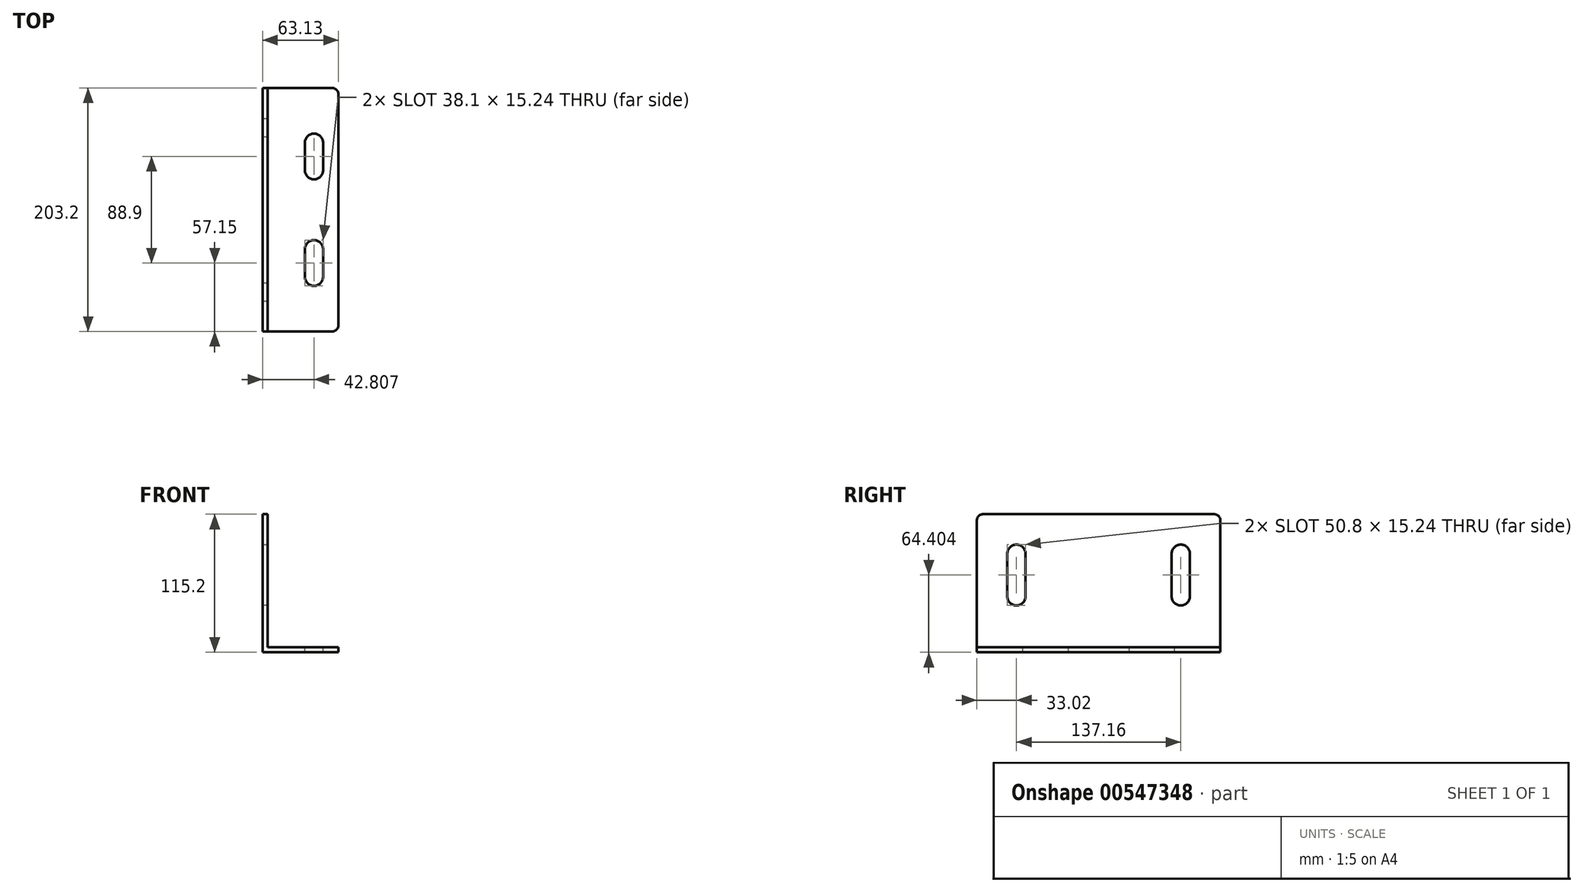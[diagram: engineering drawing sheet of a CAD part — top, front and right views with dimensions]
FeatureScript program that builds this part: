
annotation { "Feature Type Name" : "Feature", "Feature Type Description" : "" }
export const myFeature = defineFeature(function(context is Context, id is Id, definition is map)
    precondition{}
    {
        {
            var Q0;
            Q0=qCreatedBy(makeId("Front.planeOp"),FACE);
            var sketch = newSketch(context, id + "F0", { "sketchPlane" : qUnion([Q0])});
            skLineSegment(sketch, "E0", {"start": v(0, 0) * mm, "end": v(0, 111.1) * mm});
            skLineSegment(sketch, "E1", {"start": v(0, 0) * mm, "end": v(59.18, 0) * mm});
            skLineSegment(sketch, "E2", {"start": v(59.18, 0) * mm, "end": v(59.18, -4.11) * mm});
            skLineSegment(sketch, "E3", {"start": v(59.18, -4.11) * mm, "end": v(-3.95, -4.11) * mm});
            skLineSegment(sketch, "E4", {"start": v(-3.95, -4.11) * mm, "end": v(-3.95, 111.1) * mm});
            skLineSegment(sketch, "E5", {"start": v(-3.95, 111.1) * mm, "end": v(0, 111.1) * mm});
            skSolve(sketch);
        }
        {
            var Q0;
            Q0=makeQuery(id+"F0.imprint","IMPRINT",FACE,{"disambiguationData":[TD([[makeQuery(id+"F0.imprint","IMPRINT",EDGE,{"derivedFrom":sQuery(id+"F0.wireOp",EDGE,"E0")}),1.0]])]});
            extrude(context, id + "F1", {"entities" : qUnion([Q0]), "depth" : 203.2 * mm, "offsetDistance" : 25.4 * mm});
        }
        {
            var Q0;
            Q0=makeQuery(id+"F1.opExtrude","CAP_EDGE",EDGE,{"disambiguationData":[OSD([sQuery(id+"F0.wireOp",EDGE,"E5")])],"isStart":false});
            var Q1;
            Q1=makeQuery(id+"F1.opExtrude","CAP_EDGE",EDGE,{"disambiguationData":[OSD([sQuery(id+"F0.wireOp",EDGE,"E2")])],"isStart":false});
            var Q2;
            Q2=makeQuery(id+"F1.opExtrude","CAP_EDGE",EDGE,{"disambiguationData":[OSD([sQuery(id+"F0.wireOp",EDGE,"E2")])],"isStart":true});
            var Q3;
            Q3=makeQuery(id+"F1.opExtrude","CAP_EDGE",EDGE,{"disambiguationData":[OSD([sQuery(id+"F0.wireOp",EDGE,"E5")])],"isStart":true});
            fillet(context, id + "F2", {"entities" : qUnion([Q0, Q1, Q2, Q3]), "radius" : 5.08 * mm, "tangentPropagation" : true, "allowEdgeOverflow" : false});
        }
        {
            var Q0;
            Q0=makeQuery(id+"F1.opExtrude","SWEPT_FACE",FACE,{"disambiguationData":[OSD([sQuery(id+"F0.wireOp",EDGE,"E0")])]});
            var sketch = newSketch(context, id + "F3", { "sketchPlane" : qUnion([Q0])});
            skLineSegment(sketch, "E6.bottom", {"start": v(-177.8, 85.7) * mm, "end": v(-162.56, 85.7) * mm});
            skLineSegment(sketch, "E6.top", {"start": v(-177.8, 34.9) * mm, "end": v(-162.56, 34.9) * mm});
            skLineSegment(sketch, "E6.left", {"start": v(-177.8, 85.7) * mm, "end": v(-177.8, 34.9) * mm});
            skLineSegment(sketch, "E6.right", {"start": v(-162.56, 85.7) * mm, "end": v(-162.56, 34.9) * mm});
            skLineSegment(sketch, "E7.bottom", {"start": v(-40.64, 85.7) * mm, "end": v(-25.4, 85.7) * mm});
            skLineSegment(sketch, "E7.top", {"start": v(-40.64, 34.9) * mm, "end": v(-25.4, 34.9) * mm});
            skLineSegment(sketch, "E7.left", {"start": v(-40.64, 85.7) * mm, "end": v(-40.64, 34.9) * mm});
            skLineSegment(sketch, "E7.right", {"start": v(-25.4, 85.7) * mm, "end": v(-25.4, 34.9) * mm});
            skSolve(sketch);
        }
        {
            var Q0;
            Q0=makeQuery(id+"F3.imprint","IMPRINT",FACE,{"disambiguationData":[TD([[makeQuery(id+"F3.imprint","IMPRINT",EDGE,{"derivedFrom":sQuery(id+"F3.wireOp",EDGE,"E6.bottom")}),-1.0]])]});
            var Q1;
            Q1=makeQuery(id+"F3.imprint","IMPRINT",FACE,{"disambiguationData":[TD([[makeQuery(id+"F3.imprint","IMPRINT",EDGE,{"derivedFrom":sQuery(id+"F3.wireOp",EDGE,"E7.bottom")}),-1.0]])]});
            extrude(context, id + "F4", {"entities" : qUnion([Q0, Q1]), "operationType" : NewBodyOperationType.REMOVE, "endBound" : BoundingType.UP_TO_NEXT, "oppositeDirection" : true, "depth" : 25.4 * mm, "offsetDistance" : 25.4 * mm});
        }
        {
            var Q0;
            Q0=makeQuery(id+"F4.boolean.opBoolean","COPY",EDGE,{"derivedFrom":makeQuery(id+"F4.opExtrude","SWEPT_EDGE",EDGE,{"disambiguationData":[OSD([sQuery(id+"F3.wireOp",EDGE,"E6.top"),sQuery(id+"F3.wireOp",EDGE,"E6.left")])]})});
            var Q1;
            Q1=makeQuery(id+"F4.boolean.opBoolean","COPY",EDGE,{"derivedFrom":makeQuery(id+"F4.opExtrude","SWEPT_EDGE",EDGE,{"disambiguationData":[OSD([sQuery(id+"F3.wireOp",EDGE,"E6.top"),sQuery(id+"F3.wireOp",EDGE,"E6.right")])]})});
            var Q2;
            Q2=makeQuery(id+"F4.boolean.opBoolean","COPY",EDGE,{"derivedFrom":makeQuery(id+"F4.opExtrude","SWEPT_EDGE",EDGE,{"disambiguationData":[OSD([sQuery(id+"F3.wireOp",EDGE,"E6.bottom"),sQuery(id+"F3.wireOp",EDGE,"E6.left")])]})});
            var Q3;
            Q3=makeQuery(id+"F4.boolean.opBoolean","COPY",EDGE,{"derivedFrom":makeQuery(id+"F4.opExtrude","SWEPT_EDGE",EDGE,{"disambiguationData":[OSD([sQuery(id+"F3.wireOp",EDGE,"E6.bottom"),sQuery(id+"F3.wireOp",EDGE,"E6.right")])]})});
            var Q4;
            Q4=makeQuery(id+"F4.boolean.opBoolean","COPY",EDGE,{"derivedFrom":makeQuery(id+"F4.opExtrude","SWEPT_EDGE",EDGE,{"disambiguationData":[OSD([sQuery(id+"F3.wireOp",EDGE,"E7.bottom"),sQuery(id+"F3.wireOp",EDGE,"E7.left")])]})});
            var Q5;
            Q5=makeQuery(id+"F4.boolean.opBoolean","COPY",EDGE,{"derivedFrom":makeQuery(id+"F4.opExtrude","SWEPT_EDGE",EDGE,{"disambiguationData":[OSD([sQuery(id+"F3.wireOp",EDGE,"E7.bottom"),sQuery(id+"F3.wireOp",EDGE,"E7.right")])]})});
            var Q6;
            Q6=makeQuery(id+"F4.boolean.opBoolean","COPY",EDGE,{"derivedFrom":makeQuery(id+"F4.opExtrude","SWEPT_EDGE",EDGE,{"disambiguationData":[OSD([sQuery(id+"F3.wireOp",EDGE,"E7.top"),sQuery(id+"F3.wireOp",EDGE,"E7.left")])]})});
            var Q7;
            Q7=makeQuery(id+"F4.boolean.opBoolean","COPY",EDGE,{"derivedFrom":makeQuery(id+"F4.opExtrude","SWEPT_EDGE",EDGE,{"disambiguationData":[OSD([sQuery(id+"F3.wireOp",EDGE,"E7.top"),sQuery(id+"F3.wireOp",EDGE,"E7.right")])]})});
            fillet(context, id + "F5", {"entities" : qUnion([Q0, Q1, Q2, Q3, Q4, Q5, Q6, Q7]), "radius" : 7.62 * mm, "tangentPropagation" : true, "allowEdgeOverflow" : false});
        }
        {
            var Q0;
            Q0=makeQuery(id+"F1.opExtrude","SWEPT_FACE",FACE,{"disambiguationData":[OSD([sQuery(id+"F0.wireOp",EDGE,"E1")])]});
            var sketch = newSketch(context, id + "F6", { "sketchPlane" : qUnion([Q0])});
            skLineSegment(sketch, "E8", {"start": v(31.24, -165.1) * mm, "end": v(31.24, -127) * mm});
            skLineSegment(sketch, "E9", {"start": v(31.24, -127) * mm, "end": v(46.48, -127) * mm});
            skLineSegment(sketch, "E10", {"start": v(46.48, -127) * mm, "end": v(46.48, -165.1) * mm});
            skLineSegment(sketch, "E11", {"start": v(46.48, -165.1) * mm, "end": v(31.24, -165.1) * mm});
            skLineSegment(sketch, "E12.bottom", {"start": v(31.24, -76.2) * mm, "end": v(46.48, -76.2) * mm});
            skLineSegment(sketch, "E12.top", {"start": v(31.24, -38.1) * mm, "end": v(46.48, -38.1) * mm});
            skLineSegment(sketch, "E12.left", {"start": v(31.24, -76.2) * mm, "end": v(31.24, -38.1) * mm});
            skLineSegment(sketch, "E12.right", {"start": v(46.48, -76.2) * mm, "end": v(46.48, -38.1) * mm});
            skSolve(sketch);
        }
        {
            var Q0;
            Q0 = qSketchRegion(id + "F6", true);
            extrude(context, id + "F7", {"entities" : qUnion([Q0]), "operationType" : NewBodyOperationType.REMOVE, "endBound" : BoundingType.UP_TO_NEXT, "oppositeDirection" : true, "depth" : 25.4 * mm, "offsetDistance" : 25.4 * mm});
        }
        {
            var Q0;
            Q0=makeQuery(id+"F7.boolean.opBoolean","COPY",EDGE,{"derivedFrom":makeQuery(id+"F7.opExtrude","SWEPT_EDGE",EDGE,{"disambiguationData":[OSD([sQuery(id+"F6.wireOp",EDGE,"E8"),sQuery(id+"F6.wireOp",EDGE,"E11")])]})});
            var Q1;
            Q1=makeQuery(id+"F7.boolean.opBoolean","COPY",EDGE,{"derivedFrom":makeQuery(id+"F7.opExtrude","SWEPT_EDGE",EDGE,{"disambiguationData":[OSD([sQuery(id+"F6.wireOp",EDGE,"E10"),sQuery(id+"F6.wireOp",EDGE,"E11")])]})});
            var Q2;
            Q2=makeQuery(id+"F7.boolean.opBoolean","COPY",EDGE,{"derivedFrom":makeQuery(id+"F7.opExtrude","SWEPT_EDGE",EDGE,{"disambiguationData":[OSD([sQuery(id+"F6.wireOp",EDGE,"E8"),sQuery(id+"F6.wireOp",EDGE,"E9")])]})});
            var Q3;
            Q3=makeQuery(id+"F7.boolean.opBoolean","COPY",EDGE,{"derivedFrom":makeQuery(id+"F7.opExtrude","SWEPT_EDGE",EDGE,{"disambiguationData":[OSD([sQuery(id+"F6.wireOp",EDGE,"E9"),sQuery(id+"F6.wireOp",EDGE,"E10")])]})});
            var Q4;
            Q4=makeQuery(id+"F7.boolean.opBoolean","COPY",EDGE,{"derivedFrom":makeQuery(id+"F7.opExtrude","SWEPT_EDGE",EDGE,{"disambiguationData":[OSD([sQuery(id+"F6.wireOp",EDGE,"E12.top"),sQuery(id+"F6.wireOp",EDGE,"E12.right")])]})});
            var Q5;
            Q5=makeQuery(id+"F7.boolean.opBoolean","COPY",EDGE,{"derivedFrom":makeQuery(id+"F7.opExtrude","SWEPT_EDGE",EDGE,{"disambiguationData":[OSD([sQuery(id+"F6.wireOp",EDGE,"E12.bottom"),sQuery(id+"F6.wireOp",EDGE,"E12.right")])]})});
            var Q6;
            Q6=makeQuery(id+"F7.boolean.opBoolean","COPY",EDGE,{"derivedFrom":makeQuery(id+"F7.opExtrude","SWEPT_EDGE",EDGE,{"disambiguationData":[OSD([sQuery(id+"F6.wireOp",EDGE,"E12.bottom"),sQuery(id+"F6.wireOp",EDGE,"E12.left")])]})});
            var Q7;
            Q7=makeQuery(id+"F7.boolean.opBoolean","COPY",EDGE,{"derivedFrom":makeQuery(id+"F7.opExtrude","SWEPT_EDGE",EDGE,{"disambiguationData":[OSD([sQuery(id+"F6.wireOp",EDGE,"E12.top"),sQuery(id+"F6.wireOp",EDGE,"E12.left")])]})});
            fillet(context, id + "F8", {"entities" : qUnion([Q0, Q1, Q2, Q3, Q4, Q5, Q6, Q7]), "radius" : 7.62 * mm, "tangentPropagation" : true, "allowEdgeOverflow" : false});
        }
    });
